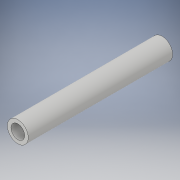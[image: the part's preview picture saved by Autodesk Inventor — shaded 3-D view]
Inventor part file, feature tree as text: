
AUTODESK INVENTOR PART (.ipt)
format: ipt  version: 2018 (Build 220112000, 112)  size: 94,208 bytes
history: native  units: mm
features: extrude x1, sketch x1
ambient origin geometry x8: Origin, YZ Plane, XZ Plane, XY Plane, X Axis, Y Axis, Z Axis, Center Point
bodies: Volumenkörper1 (feature_tree)
feature tree (2):
  extrude  "Extrusion1"  Depth=40.0mm
  sketch  "Skizze1"  dims[d0=3.8mm d1=1.0mm d2=40.0mm d3=0.0mm]
